# Revit family: MARK Product_ Studioscape_ Sofa Family
name_source: partatom
category: Furniture
revit_build: Autodesk Revit 2018 (Build: 20170223_1515(x64)
units: mm (PartAtom-declared; Revit-internal decimal feet)

## family parameters
Always vertical = Yes
Cut with Voids When Loaded = No
OmniClass Number = 23.40.20.00
OmniClass Title = General Furniture and Specialties
Room Calculation Point = No
Shared = No
Work Plane-Based = No

## types (9) — shared parameters
FabricMaterial = Fabric (Signal Red)
SledMaterial = Powder Coat (Tele Grey)
Surface Material = Oak

## per-type parameters (varying)
| type | Furniture Type |
| Corner Sofa 1125 Square Back (1125X680X380) | StudioCornerSofaSquare1125 : Corner Sofa |
| Corner Sofa 1125 Round Back (1125X1125X680X380) | StudioCornerSofa1125 : Corner Sofa |
| Sofa (750X750X680X380) | StudioSofa : Sofa 750 Wide |
| Sofa (1125X750X680X380) | StudioSofa : Sofa 1125 Wide |
| Sofa (1500X750X680X380) | StudioSofa : Sofa 1500 Wide |
| Sofa Corner (750X750X680X380) | StudioCornerSofa : Corner Sofa |
| Bench (750X750X380X380) | StudioBench : Bench 750 Wide |
| Bench (1125X750X380X380) | StudioBench : Bench 1125 Wide |
| Bench (1500X750X380X380) | StudioBench : Bench 1500 Wide |

## geometry (parser evidence)
native form markers: Sweep x85
no freeform markers — native parametric forms only
